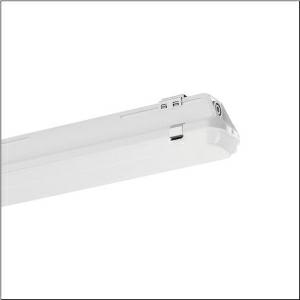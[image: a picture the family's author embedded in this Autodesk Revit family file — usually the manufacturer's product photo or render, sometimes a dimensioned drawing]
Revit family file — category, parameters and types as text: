
# Revit family: monsun_11_51fp10mp4b0u
name_source: partatom
category: Lighting Fixtures
units: mm (PartAtom-declared; Revit-internal decimal feet)

## family parameters
Cut with Voids When Loaded = No
Host = Face
Light Source = No
Part Type = Normal
Room Calculation Point = No
Round Connector Dimension = Use Diameter
Shared = No

## types (1)
- --- (1 x LED, 12070 lm, 62.4 W, 4000K)
    Apparent Load = 62 VA
    CIE Flux Codes = 47 76 93 94 100
    Color Rendering = 80
    Color Temperature = 4000K
    Default Elevation = 1800 mm
    Description = Monsun 11, damp-proof luminaire, chain hanger, primary optical cover: enclosure, of PMMA, light emission: direct distribution, primary light characteristic: symmetric, installation type: suspended mounting, surface-mounted, horizontal mounting, vertical mounting, LED, rated luminous flux: 12.070lm, luminous efficacy: 193lm/W, light colour: 840, colour temperature: 4000K, control gear: ON/OFF Multilumen, with terminal, 3-pole, max. 2.5mm², mains connection: 220..240V, AC, 50/60Hz, rated input power: 62W, luminaire housing, of glass-fibre reinforced polyester, uncoated, bright grey, incl. chain hanger, length: 1.590mm, width: 90mm, height: 88mm, clip for enclosure, of stainless steel (V2A), ceiling mounting element, of stainless steel (V2A), chain hanger, of stainless steel (V2A), protection rating (complete): IP66, insulation class (complete): insulation class I (protective earthing), certification: CE, ENEC, VDE, UKCA, protection symbol: D, impact resistance: IK04, permissible operating ambient temperature: -35..+35°C, standard: EN 50419, EN 60598-2-1, contact your sales advisor before using the luminaires in applications with unclear chemical exposure, large temperature fluctuations or condensation-forming humidity, LABS conformity tested according to VDMA 24364:2018-05, no direct snow, no direct sun, no direct rain, for indoor or canopied outdoor use, corresponds to IFS (International Featured Standards) requirements for safety and quality in the food industry, packaging unit: 1 piece
    Height = 89 mm
    Lamp = 1 x LED
    Lamp Light Flux = 12070 lm
    Lamp Power = 62.4 W
    Lamp count = 1
    Length = 1590 mm
    Luminous efficacy = 193 lm/W
    Manufacturer = Siteco
    ModVariant = No
    Model = 51FP10MP4B0U
    Mounting Place = Ceiling
    Mounting Type = Surface mounted
    Number of Poles = 1
    OnlyDefault = Yes
    Power Factor = 1
    Product Name = Monsun 11
    Product group = damp-proof luminaire
    ProductGroupID = 300
    Protection Class = Protection class I
    Protection Degree = IP 66
    RLX_Detail_Level = 1
    RLX_Emergency_Light_Flux = 0 lm
    RLX_Emergency_Type = 0
    RLX_Emergency_Type_DB = No
    RlxData = <blob elided: 89957 chars, md5=79c9f264>
    Socket = socket
    Standby Power = 0 W
    System Light Flux = 12070 lm
    System Power = 62 W
    Type Comments = factory setting: luminous flux: 100 % | (A | C | E) | 147 mA
    Type Image = l_1349237.jpg
    URL = http://relux.com
    VarID = @adj_000065
    Voltage = 0 V
    Weight = 0.00 kg
    Width = 90 mm

## geometry (parser evidence)
native form markers: Blend x4, Sweep x14
no freeform markers — native parametric forms only
